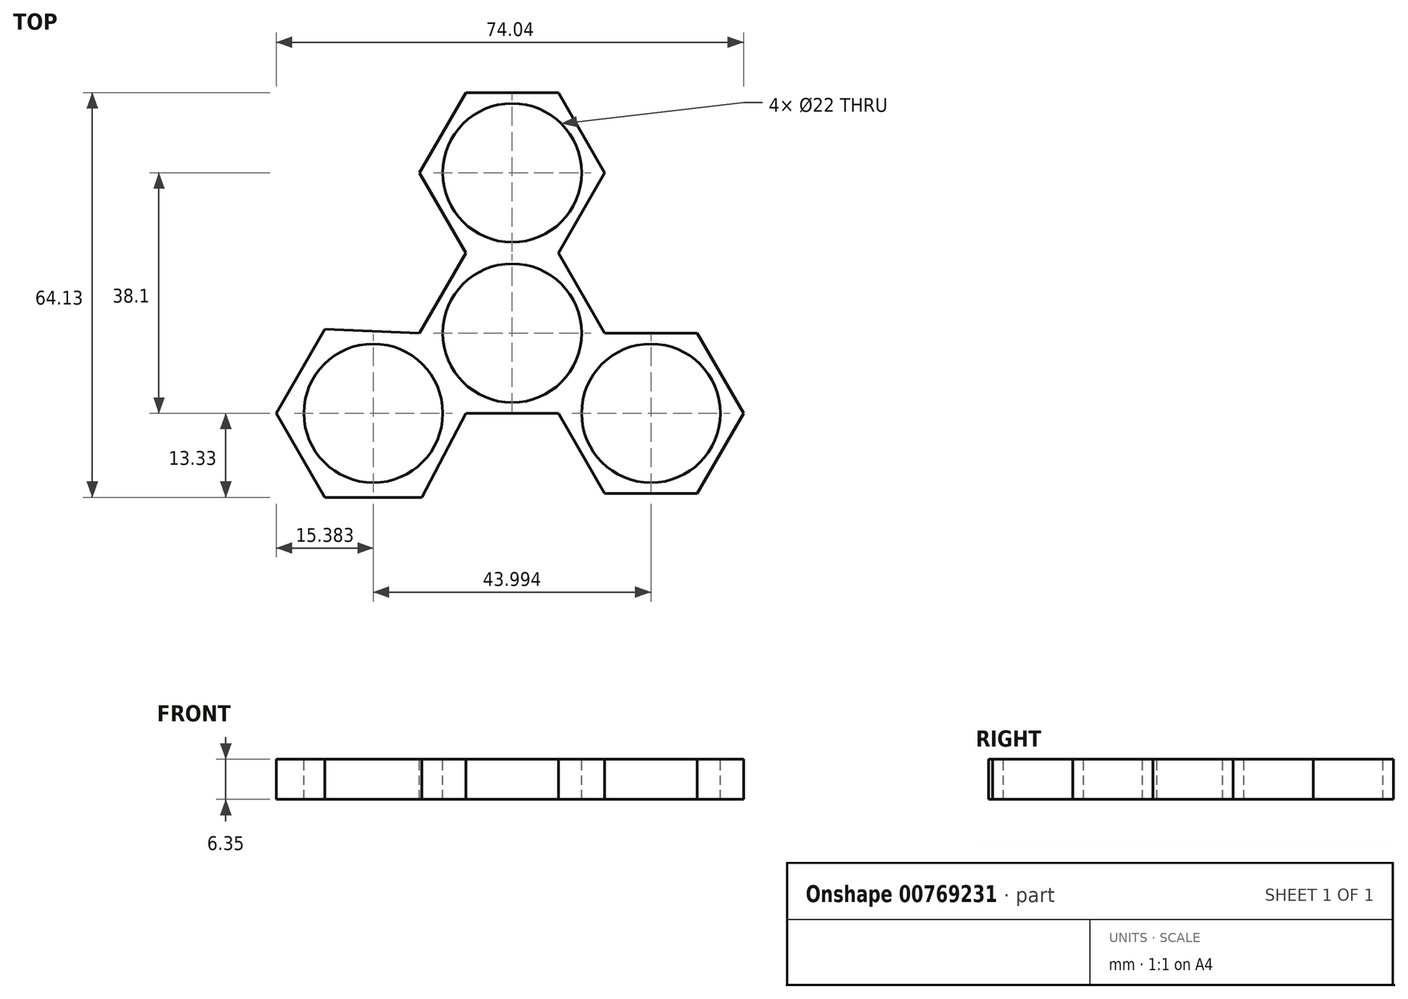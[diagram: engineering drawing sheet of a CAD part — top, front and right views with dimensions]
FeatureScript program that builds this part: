
annotation { "Feature Type Name" : "Feature", "Feature Type Description" : "" }
export const myFeature = defineFeature(function(context is Context, id is Id, definition is map)
    precondition{}
    {
        {
            var Q0;
            Q0=qCreatedBy(makeId("Top.planeOp"),FACE);
            var sketch = newSketch(context, id + "F0", { "sketchPlane" : qUnion([Q0])});
            skCircle(sketch, "E0", {"center": v(0, 0) * mm, "radius": 11 * mm});
            skCircle(sketch, "E1", {"center": v(0, 25.4) * mm, "radius": 11 * mm});
            skCircle(sketch, "E2", {"center": v(22, -12.7) * mm, "radius": 11 * mm});
            skCircle(sketch, "E3", {"center": v(-22, -12.7) * mm, "radius": 11 * mm});
            skLineSegment(sketch, "E4.0", {"start": v(7.33, -12.7) * mm, "end": v(-7.33, -12.7) * mm});
            skLineSegment(sketch, "E4.2", {"start": v(-14.66, 0) * mm, "end": v(-7.33, 12.7) * mm});
            skLineSegment(sketch, "E4.4", {"start": v(7.33, 12.7) * mm, "end": v(14.66, 0) * mm});
            skPoint(sketch, "E4.0.midPoint", {"position": v(0, -12.7) * mm});
            skLineSegment(sketch, "E5.1", {"start": v(-14.3, -26.03) * mm, "end": v(-29.7, -26.03) * mm});
            skLineSegment(sketch, "E5.2", {"start": v(-29.7, -26.03) * mm, "end": v(-37.38, -12.7) * mm});
            skLineSegment(sketch, "E5.3", {"start": v(-37.38, -12.7) * mm, "end": v(-29.7, 0.63) * mm});
            skLineSegment(sketch, "E6", {"start": v(-14.3, -26.03) * mm, "end": v(-7.33, -12.7) * mm});
            skLineSegment(sketch, "E7", {"start": v(-29.7, 0.63) * mm, "end": v(-14.66, 0) * mm});
            skLineSegment(sketch, "E8.2", {"start": v(29.33, 0) * mm, "end": v(36.66, -12.7) * mm});
            skLineSegment(sketch, "E8.3", {"start": v(36.66, -12.7) * mm, "end": v(29.33, -25.4) * mm});
            skLineSegment(sketch, "E8.4", {"start": v(29.33, -25.4) * mm, "end": v(14.66, -25.4) * mm});
            skLineSegment(sketch, "E9.2", {"start": v(-14.66, 25.4) * mm, "end": v(-7.33, 38.1) * mm});
            skLineSegment(sketch, "E9.3", {"start": v(-7.33, 38.1) * mm, "end": v(7.33, 38.1) * mm});
            skLineSegment(sketch, "E9.4", {"start": v(7.33, 38.1) * mm, "end": v(14.66, 25.4) * mm});
            skLineSegment(sketch, "E10", {"start": v(14.66, 25.4) * mm, "end": v(7.33, 12.7) * mm});
            skLineSegment(sketch, "E11", {"start": v(-14.66, 25.4) * mm, "end": v(-7.33, 12.7) * mm});
            skLineSegment(sketch, "E12", {"start": v(29.33, 0) * mm, "end": v(14.66, 0) * mm});
            skLineSegment(sketch, "E13", {"start": v(14.66, -25.4) * mm, "end": v(7.33, -12.7) * mm});
            skSolve(sketch);
        }
        {
            var Q0;
            Q0=makeQuery(id+"F0.imprint","IMPRINT",FACE,{"disambiguationData":[TD([[makeQuery(id+"F0.imprint","IMPRINT",EDGE,{"derivedFrom":sQuery(id+"F0.wireOp",EDGE,"E0")}),-1.0]])]});
            extrude(context, id + "F1", {"entities" : qUnion([Q0]), "oppositeDirection" : true, "depth" : 6.35 * mm, "offsetDistance" : 25.4 * mm});
        }
    });
